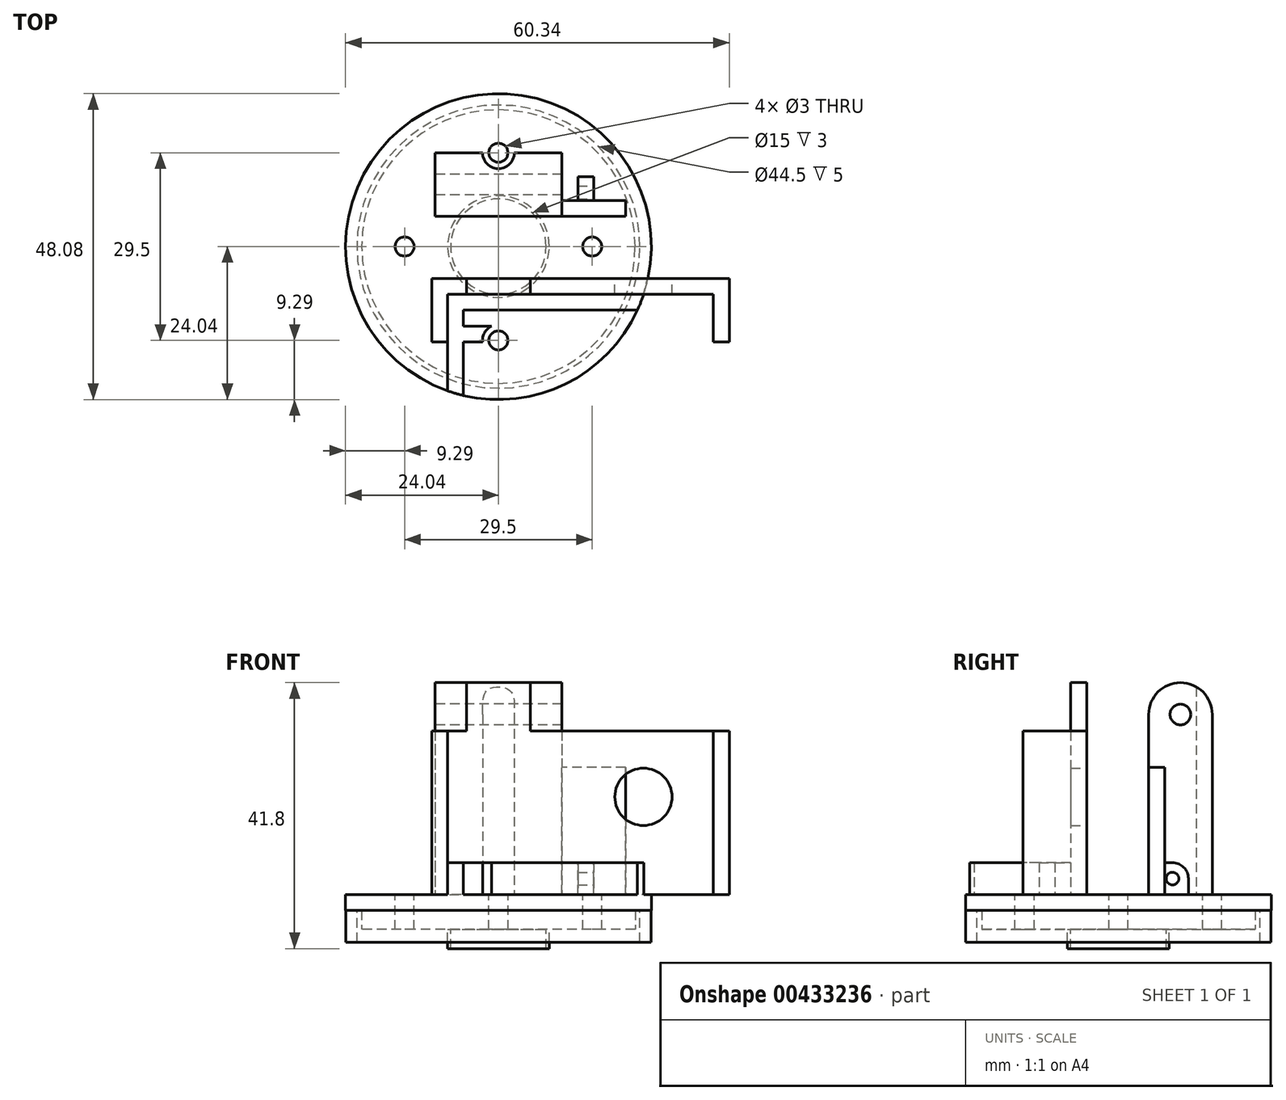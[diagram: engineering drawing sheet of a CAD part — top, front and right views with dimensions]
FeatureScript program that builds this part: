
annotation { "Feature Type Name" : "Feature", "Feature Type Description" : "" }
export const myFeature = defineFeature(function(context is Context, id is Id, definition is map)
    precondition{}
    {
        {
            var Q0;
            Q0=qCreatedBy(makeId("Top.planeOp"),FACE);
            var sketch = newSketch(context, id + "F0", { "sketchPlane" : qUnion([Q0])});
            skCircle(sketch, "E0", {"center": v(0, 0) * mm, "radius": 21.5 * mm});
            skSolve(sketch);
        }
        {
            var Q0;
            Q0 = qSketchRegion(id + "F0", true);
            extrude(context, id + "F1", {"entities" : qUnion([Q0]), "depth" : 3 * mm});
        }
        {
            var Q0;
            Q0=makeQuery(id+"F1.opExtrude","CAP_FACE",FACE,{"disambiguationData":[OSD([sQuery(id+"F0.wireOp",EDGE,"E0")])],"isStart":false});
            var sketch = newSketch(context, id + "F2", { "sketchPlane" : qUnion([Q0])});
            skLineSegment(sketch, "E1", {"start": v(0, 0) * mm, "end": v(14.75, 0) * mm, "construction": true});
            skLineSegment(sketch, "E2", {"start": v(0, 0) * mm, "end": v(0, -14.75) * mm, "construction": true});
            skLineSegment(sketch, "E3", {"start": v(0, 0) * mm, "end": v(-14.75, 0) * mm, "construction": true});
            skCircle(sketch, "E4", {"center": v(0, 14.75) * mm, "radius": 1.5 * mm});
            skCircle(sketch, "E5", {"center": v(-14.75, 0) * mm, "radius": 1.5 * mm});
            skCircle(sketch, "E6", {"center": v(14.75, 0) * mm, "radius": 1.5 * mm});
            skCircle(sketch, "E7", {"center": v(0, -14.75) * mm, "radius": 1.5 * mm});
            skLineSegment(sketch, "E8", {"start": v(0, 14.75) * mm, "end": v(0, 0) * mm, "construction": true});
            skSolve(sketch);
        }
        {
            var Q0;
            Q0 = qSketchRegion(id + "F2", true);
            extrude(context, id + "F3", {"entities" : qUnion([Q0]), "operationType" : NewBodyOperationType.REMOVE, "endBound" : BoundingType.UP_TO_NEXT, "oppositeDirection" : true, "depth" : 25 * mm});
        }
        {
            var Q0;
            Q0=makeQuery(id+"F1.opExtrude","CAP_FACE",FACE,{"disambiguationData":[OSD([sQuery(id+"F0.wireOp",EDGE,"E0")])],"isStart":false});
            var sketch = newSketch(context, id + "F4", { "sketchPlane" : qUnion([Q0])});
            skCircle(sketch, "E9", {"center": v(0, 0) * mm, "radius": 24 * mm});
            skCircle(sketch, "E10", {"center": v(0, 0) * mm, "radius": 22.25 * mm});
            skSolve(sketch);
        }
        {
            var Q0;
            Q0 = qSketchRegion(id + "F4", true);
            extrude(context, id + "F5", {"entities" : qUnion([Q0]), "oppositeDirection" : true, "depth" : 5 * mm});
        }
        {
            var Q0;
            Q0=makeQuery(id+"F5.opExtrude","CAP_FACE",FACE,{"disambiguationData":[OSD([sQuery(id+"F4.wireOp",EDGE,"E9"),sQuery(id+"F4.wireOp",EDGE,"E10")])],"isStart":true});
            var sketch = newSketch(context, id + "F6", { "sketchPlane" : qUnion([Q0])});
            skCircle(sketch, "E11", {"center": v(0, 0) * mm, "radius": 24.04 * mm});
            skLineSegment(sketch, "E12", {"start": v(0, 0) * mm, "end": v(0, 14.75) * mm, "construction": true});
            skLineSegment(sketch, "E13", {"start": v(0, 0) * mm, "end": v(14.75, 0) * mm, "construction": true});
            skLineSegment(sketch, "E14.MirrorCS", {"start": v(0, 0) * mm, "end": v(0, -14.75) * mm, "construction": true});
            skLineSegment(sketch, "E15.MirrorCS", {"start": v(0, 0) * mm, "end": v(-14.75, 0) * mm, "construction": true});
            skCircle(sketch, "E16", {"center": v(0, 14.75) * mm, "radius": 1.5 * mm});
            skCircle(sketch, "E17", {"center": v(14.75, 0) * mm, "radius": 1.5 * mm});
            skCircle(sketch, "E18.MirrorC", {"center": v(0, -14.75) * mm, "radius": 1.5 * mm});
            skCircle(sketch, "E19.MirrorC", {"center": v(-14.75, 0) * mm, "radius": 1.5 * mm});
            skSolve(sketch);
        }
        {
            var Q0;
            Q0=makeQuery(id+"F1.opExtrude","CAP_FACE",FACE,{"disambiguationData":[OSD([sQuery(id+"F0.wireOp",EDGE,"E0")])],"isStart":true});
            var sketch = newSketch(context, id + "F7", { "sketchPlane" : qUnion([Q0])});
            skCircle(sketch, "E20", {"center": v(0, 0) * mm, "radius": 8 * mm});
            skCircle(sketch, "E21", {"center": v(0, 0) * mm, "radius": 7.5 * mm});
            skSolve(sketch);
        }
        {
            var Q0;
            Q0 = qSketchRegion(id + "F7", true);
            extrude(context, id + "F8", {"entities" : qUnion([Q0]), "operationType" : NewBodyOperationType.ADD, "depth" : 3 * mm});
        }
        {
            var Q0;
            Q0 = qSketchRegion(id + "F6", true);
            extrude(context, id + "F9", {"entities" : qUnion([Q0]), "operationType" : NewBodyOperationType.ADD, "depth" : 2.5 * mm});
        }
        {
            var Q0;
            Q0=makeQuery(id+"F9.opExtrude","CAP_FACE",FACE,{"disambiguationData":[OSD([sQuery(id+"F6.wireOp",EDGE,"E11"),sQuery(id+"F6.wireOp",EDGE,"E16"),sQuery(id+"F6.wireOp",EDGE,"E17"),sQuery(id+"F6.wireOp",EDGE,"E18.MirrorC"),sQuery(id+"F6.wireOp",EDGE,"E19.MirrorC")])],"isStart":false});
            var sketch = newSketch(context, id + "F10", { "sketchPlane" : qUnion([Q0])});
            skLineSegment(sketch, "E22", {"start": v(0, 0) * mm, "end": v(0, -5) * mm, "construction": true});
            skLineSegment(sketch, "E23", {"start": v(0, -5) * mm, "end": v(-8, -5) * mm, "construction": true});
            skLineSegment(sketch, "E24.bottom", {"start": v(-8, -5) * mm, "end": v(33.8, -5) * mm});
            skLineSegment(sketch, "E24.top", {"start": v(-8, -7.5) * mm, "end": v(33.8, -7.5) * mm});
            skLineSegment(sketch, "E24.left", {"start": v(-8, -5) * mm, "end": v(-8, -7.5) * mm});
            skLineSegment(sketch, "E24.right", {"start": v(33.8, -5) * mm, "end": v(33.8, -7.5) * mm});
            skLineSegment(sketch, "E25.bottom", {"start": v(-8, -5) * mm, "end": v(-10.5, -5) * mm});
            skLineSegment(sketch, "E25.top", {"start": v(-8, -15) * mm, "end": v(-10.5, -15) * mm});
            skLineSegment(sketch, "E25.left", {"start": v(-8, -5) * mm, "end": v(-8, -15) * mm});
            skLineSegment(sketch, "E25.right", {"start": v(-10.5, -5) * mm, "end": v(-10.5, -15) * mm});
            skLineSegment(sketch, "E26.bottom", {"start": v(33.8, -5) * mm, "end": v(36.3, -5) * mm});
            skLineSegment(sketch, "E26.top", {"start": v(33.8, -15) * mm, "end": v(36.3, -15) * mm});
            skLineSegment(sketch, "E26.left", {"start": v(33.8, -5) * mm, "end": v(33.8, -15) * mm});
            skLineSegment(sketch, "E26.right", {"start": v(36.3, -5) * mm, "end": v(36.3, -15) * mm});
            skSolve(sketch);
        }
        {
            var Q0;
            Q0 = qSketchRegion(id + "F10", true);
            extrude(context, id + "F11", {"entities" : qUnion([Q0]), "operationType" : NewBodyOperationType.ADD, "depth" : 25.7 * mm});
        }
        {
            var Q0;
            Q0=makeQuery(id+"F11.opExtrude","SWEPT_FACE",FACE,{"disambiguationData":[OSD([sQuery(id+"F10.wireOp",EDGE,"E24.bottom"),sQuery(id+"F10.wireOp",EDGE,"E25.bottom"),sQuery(id+"F10.wireOp",EDGE,"E26.bottom")])]});
            var sketch = newSketch(context, id + "F12", { "sketchPlane" : qUnion([Q0])});
            skLineSegment(sketch, "E27.MirrorCS", {"start": v(-36.3, 20.85) * mm, "end": v(-27.3, 20.85) * mm, "construction": true});
            skLineSegment(sketch, "E28.MirrorCS", {"start": v(-36.3, 10.5) * mm, "end": v(-36.3, 31.2) * mm, "construction": true});
            skLineSegment(sketch, "E29.MirrorCS", {"start": v(-36.3, 5.5) * mm, "end": v(-36.3, 10.5) * mm, "construction": true});
            skLineSegment(sketch, "E30", {"start": v(-27.3, 20.85) * mm, "end": v(-22.8, 20.85) * mm, "construction": true});
            skCircle(sketch, "E31", {"center": v(-22.8, 20.85) * mm, "radius": 4.5 * mm});
            skSolve(sketch);
        }
        {
            var Q0;
            Q0=makeQuery(id+"F12.imprint","IMPRINT",FACE,{"disambiguationData":[TD([[makeQuery(id+"F12.imprint","IMPRINT",EDGE,{"derivedFrom":sQuery(id+"F12.wireOp",EDGE,"E31")}),1.0]])]});
            var Q1;
            Q1=makeQuery(id+"F11.opExtrude","SWEPT_FACE",FACE,{"disambiguationData":[OSD([sQuery(id+"F10.wireOp",EDGE,"E24.top")])]});
            extrude(context, id + "F13", {"entities" : qUnion([Q0]), "operationType" : NewBodyOperationType.REMOVE, "endBound" : BoundingType.UP_TO_SURFACE, "oppositeDirection" : true, "endBoundEntityFace" : qUnion([Q1]), "depth" : 25 * mm});
        }
        {
            var Q0;
            Q0=makeQuery(id+"F9.opExtrude","CAP_FACE",FACE,{"disambiguationData":[OSD([sQuery(id+"F6.wireOp",EDGE,"E11"),sQuery(id+"F6.wireOp",EDGE,"E16"),sQuery(id+"F6.wireOp",EDGE,"E17"),sQuery(id+"F6.wireOp",EDGE,"E18.MirrorC"),sQuery(id+"F6.wireOp",EDGE,"E19.MirrorC")])],"isStart":false});
            var sketch = newSketch(context, id + "F14", { "sketchPlane" : qUnion([Q0])});
            skLineSegment(sketch, "E32", {"start": v(-8, -15) * mm, "end": v(18.79, -15) * mm});
            skLineSegment(sketch, "E33", {"start": v(-8, -15) * mm, "end": v(-8, -12.5) * mm});
            skLineSegment(sketch, "E34", {"start": v(-8, -12.5) * mm, "end": v(20.53, -12.5) * mm});
            skLineSegment(sketch, "E35", {"start": v(-8, -12.5) * mm, "end": v(-5.5, -12.5) * mm, "construction": true});
            skCircle(sketch, "E36", {"center": v(0, -14.75) * mm, "radius": 2.5 * mm});
            skLineSegment(sketch, "E37", {"start": v(-5.5, -12.5) * mm, "end": v(-5.5, -7.5) * mm});
            skLineSegment(sketch, "E38", {"start": v(-5.5, -7.5) * mm, "end": v(-5.5, -10) * mm, "construction": true});
            skLineSegment(sketch, "E39", {"start": v(-5.5, -10) * mm, "end": v(21.86, -10) * mm});
            skLineSegment(sketch, "E40", {"start": v(20.53, -12.5) * mm, "end": v(18.03, -12.5) * mm});
            skLineSegment(sketch, "E41", {"start": v(21.86, -10) * mm, "end": v(19.36, -10) * mm});
            skLineSegment(sketch, "E42", {"start": v(19.36, -10) * mm, "end": v(18.03, -12.5) * mm});
            skLineSegment(sketch, "E43", {"start": v(-8, -15) * mm, "end": v(-8, -22.67) * mm});
            skLineSegment(sketch, "E44", {"start": v(-5.5, -12.5) * mm, "end": v(-5.5, -23.4) * mm});
            skSolve(sketch);
        }
        {
            var Q0;
            {var subQ1=sQuery(id+"F14.wireOp",EDGE,"E33");Q0=makeQuery(id+"F14.imprint","IMPRINT",FACE,{"disambiguationData":[TD([[makeQuery(id+"F14.imprint","IMPRINT",EDGE,{"derivedFrom":subQ1}),1.0]])]});}
            var Q1;
            {var subQ0=sQuery(id+"F14.wireOp",EDGE,"E37");var subQ1=sQuery(id+"F14.wireOp",EDGE,"E34");var subQ2=makeQuery(id+"F14.imprint","INTERSECT",VERTEX,{"derivedFrom":[subQ1,subQ0]});Q1=makeQuery(id+"F14.imprint","IMPRINT",FACE,{"disambiguationData":[TD([[makeQuery(id+"F14.imprint","IMPRINT",EDGE,{"disambiguationData":[TD([[subQ2,-1.0]])],"derivedFrom":subQ0}),1.0]])]});}
            var Q2;
            {var subQ7=sQuery(id+"F14.wireOp",EDGE,"E39");Q2=makeQuery(id+"F14.imprint","IMPRINT",FACE,{"disambiguationData":[TD([[makeQuery(id+"F14.imprint","IMPRINT",EDGE,{"derivedFrom":subQ7}),1.0]])]});}
            var Q3;
            {var subQ0=sQuery(id+"F14.wireOp",EDGE,"E40");Q3=makeQuery(id+"F14.imprint","IMPRINT",FACE,{"disambiguationData":[TD([[makeQuery(id+"F14.imprint","IMPRINT",EDGE,{"derivedFrom":subQ0}),-1.0]])]});}
            var Q4;
            {var subQ0=sQuery(id+"F14.wireOp",EDGE,"E40");Q4=makeQuery(id+"F14.imprint","IMPRINT",FACE,{"disambiguationData":[TD([[makeQuery(id+"F14.imprint","IMPRINT",EDGE,{"derivedFrom":subQ0}),1.0]])]});}
            var Q5;
            {var subQ0=sQuery(id+"F14.wireOp",EDGE,"E43");Q5=makeQuery(id+"F14.imprint","IMPRINT",FACE,{"disambiguationData":[TD([[makeQuery(id+"F14.imprint","IMPRINT",EDGE,{"derivedFrom":subQ0}),1.0]])]});}
            var Q6;
            {var subQ0=sQuery(id+"F14.wireOp",EDGE,"E44");var subQ1=sQuery(id+"F14.wireOp",EDGE,"E32");var subQ2=makeQuery(id+"F14.imprint","INTERSECT",VERTEX,{"derivedFrom":[subQ1,subQ0]});Q6=makeQuery(id+"F14.imprint","IMPRINT",FACE,{"disambiguationData":[TD([[makeQuery(id+"F14.imprint","IMPRINT",EDGE,{"disambiguationData":[TD([[subQ2,-1.0]])],"derivedFrom":subQ1}),1.0]])]});}
            extrude(context, id + "F15", {"entities" : qUnion([Q0, Q1, Q2, Q3, Q4, Q5, Q6]), "operationType" : NewBodyOperationType.ADD, "depth" : 5 * mm});
        }
        {
            var Q0;
            {var subQ8=sQuery(id+"F6.wireOp",EDGE,"E11");var subQ10=sQuery(id+"F6.wireOp",EDGE,"E16");var subQ11=sQuery(id+"F6.wireOp",EDGE,"E17");var subQ12=sQuery(id+"F6.wireOp",EDGE,"E19.MirrorC");var subQ13=makeQuery(id+"F9.opExtrude","CAP_FACE",FACE,{"disambiguationData":[OSD([subQ8,subQ10,subQ11,sQuery(id+"F6.wireOp",EDGE,"E18.MirrorC"),subQ12])],"isStart":false});Q0=makeQuery(id+"F15.boolean.opBoolean","SPLIT",FACE,{"disambiguationData":[TD([makeQuery(id+"F9.opExtrude","SWEPT_FACE",FACE,{"disambiguationData":[OSD([subQ10])]})])],"derivedFrom":subQ13});}
            var sketch = newSketch(context, id + "F16", { "sketchPlane" : qUnion([Q0])});
            skLineSegment(sketch, "E45", {"start": v(0, 14.75) * mm, "end": v(0, 4.75) * mm, "construction": true});
            skLineSegment(sketch, "E46", {"start": v(0, 4.75) * mm, "end": v(0, 9.75) * mm, "construction": true});
            skLineSegment(sketch, "E47.bottom", {"start": v(-10, 4.75) * mm, "end": v(10, 4.75) * mm});
            skLineSegment(sketch, "E47.top", {"start": v(-10, 14.75) * mm, "end": v(10, 14.75) * mm});
            skLineSegment(sketch, "E47.left", {"start": v(-10, 4.75) * mm, "end": v(-10, 14.75) * mm});
            skLineSegment(sketch, "E47.right", {"start": v(10, 4.75) * mm, "end": v(10, 14.75) * mm});
            skPoint(sketch, "E47.middle", {"position": v(0, 9.75) * mm});
            skCircle(sketch, "E48", {"center": v(0, 14.75) * mm, "radius": 2.5 * mm});
            skSolve(sketch);
        }
        {
            var Q0;
            Q0=makeQuery(id+"F16.imprint","IMPRINT",FACE,{"disambiguationData":[TD([[makeQuery(id+"F16.imprint","IMPRINT",EDGE,{"derivedFrom":sQuery(id+"F16.wireOp",EDGE,"E47.bottom")}),1.0]])]});
            extrude(context, id + "F17", {"entities" : qUnion([Q0]), "operationType" : NewBodyOperationType.ADD, "depth" : 33.3 * mm});
        }
        {
            var Q0;
            Q0=makeQuery(id+"F17.opExtrude","SWEPT_FACE",FACE,{"disambiguationData":[OSD([sQuery(id+"F16.wireOp",EDGE,"E47.left")])]});
            var sketch = newSketch(context, id + "F18", { "sketchPlane" : qUnion([Q0])});
            skLineSegment(sketch, "E49", {"start": v(-9.75, 38.8) * mm, "end": v(-9.75, 28.8) * mm, "construction": true});
            skPoint(sketch, "E49.endSnap0", {"position": v(-9.75, 38.8) * mm});
            skCircle(sketch, "E50", {"center": v(-9.75, 33.8) * mm, "radius": 5 * mm});
            skCircle(sketch, "E51", {"center": v(-9.75, 33.8) * mm, "radius": 1.63 * mm});
            skSolve(sketch);
        }
        {
            var Q0;
            Q0=makeQuery(id+"F18.imprint","IMPRINT",FACE,{"disambiguationData":[TD([[makeQuery(id+"F18.imprint","IMPRINT",EDGE,{"derivedFrom":sQuery(id+"F18.wireOp",EDGE,"E51")}),1.0]])]});
            var Q1;
            {var subQ0=sQuery(id+"F18.wireOp",EDGE,"E50");var subQ1=sQuery(id+"F16.wireOp",EDGE,"E47.left");var subQ2=makeQuery(id+"F17.opExtrude","CAP_EDGE",EDGE,{"disambiguationData":[OSD([subQ1])],"isStart":false});var subQ3=makeQuery(id+"F18.imprint","INTERSECT",VERTEX,{"derivedFrom":[subQ2,subQ0]});Q1=makeQuery(id+"F18.imprint","IMPRINT",FACE,{"disambiguationData":[TD([[makeQuery(id+"F18.imprint","IMPRINT",EDGE,{"disambiguationData":[TD([[subQ3,-1.0]])],"derivedFrom":subQ0}),-1.0]])]});}
            var Q2;
            {var subQ0=sQuery(id+"F18.wireOp",EDGE,"E50");var subQ1=sQuery(id+"F16.wireOp",EDGE,"E47.left");var subQ2=makeQuery(id+"F17.opExtrude","CAP_EDGE",EDGE,{"disambiguationData":[OSD([subQ1])],"isStart":false});var subQ3=makeQuery(id+"F18.imprint","INTERSECT",VERTEX,{"derivedFrom":[subQ2,subQ0]});Q2=makeQuery(id+"F18.imprint","IMPRINT",FACE,{"disambiguationData":[TD([[makeQuery(id+"F18.imprint","IMPRINT",EDGE,{"disambiguationData":[TD([[subQ3,1.0]])],"derivedFrom":subQ0}),-1.0]])]});}
            var Q3;
            Q3=makeQuery(id+"F17.opExtrude","SWEPT_FACE",FACE,{"disambiguationData":[OSD([sQuery(id+"F16.wireOp",EDGE,"E47.right")])]});
            extrude(context, id + "F19", {"entities" : qUnion([Q0, Q1, Q2]), "operationType" : NewBodyOperationType.REMOVE, "endBound" : BoundingType.UP_TO_SURFACE, "oppositeDirection" : true, "endBoundEntityFace" : qUnion([Q3]), "depth" : 25 * mm});
        }
        {
            var Q0;
            Q0=makeQuery(id+"F11.opExtrude","CAP_FACE",FACE,{"disambiguationData":[OSD([sQuery(id+"F10.wireOp",EDGE,"E24.bottom"),sQuery(id+"F10.wireOp",EDGE,"E24.top"),sQuery(id+"F10.wireOp",EDGE,"E25.bottom"),sQuery(id+"F10.wireOp",EDGE,"E25.top"),sQuery(id+"F10.wireOp",EDGE,"E25.left"),sQuery(id+"F10.wireOp",EDGE,"E25.right"),sQuery(id+"F10.wireOp",EDGE,"E26.bottom"),sQuery(id+"F10.wireOp",EDGE,"E26.top"),sQuery(id+"F10.wireOp",EDGE,"E26.left"),sQuery(id+"F10.wireOp",EDGE,"E26.right")])],"isStart":false});
            var sketch = newSketch(context, id + "F20", { "sketchPlane" : qUnion([Q0])});
            skLineSegment(sketch, "E52", {"start": v(0, 0) * mm, "end": v(0, -5) * mm, "construction": true});
            skLineSegment(sketch, "E53", {"start": v(0, -5) * mm, "end": v(-5, -5) * mm, "construction": true});
            skLineSegment(sketch, "E54.bottom", {"start": v(-5, -5) * mm, "end": v(5, -5) * mm});
            skLineSegment(sketch, "E54.top", {"start": v(-5, -7.5) * mm, "end": v(5, -7.5) * mm});
            skLineSegment(sketch, "E54.left", {"start": v(-5, -5) * mm, "end": v(-5, -7.5) * mm});
            skLineSegment(sketch, "E54.right", {"start": v(5, -5) * mm, "end": v(5, -7.5) * mm});
            skSolve(sketch);
        }
        {
            var Q0;
            Q0 = qSketchRegion(id + "F20", true);
            extrude(context, id + "F21", {"entities" : qUnion([Q0]), "operationType" : NewBodyOperationType.ADD, "depth" : 7.6 * mm});
        }
        {
            var Q0;
            {var subQ8=sQuery(id+"F6.wireOp",EDGE,"E11");var subQ10=sQuery(id+"F6.wireOp",EDGE,"E16");var subQ11=sQuery(id+"F6.wireOp",EDGE,"E17");var subQ12=sQuery(id+"F6.wireOp",EDGE,"E19.MirrorC");var subQ13=makeQuery(id+"F9.opExtrude","CAP_FACE",FACE,{"disambiguationData":[OSD([subQ8,subQ10,subQ11,sQuery(id+"F6.wireOp",EDGE,"E18.MirrorC"),subQ12])],"isStart":false});Q0=makeQuery(id+"F15.boolean.opBoolean","SPLIT",FACE,{"disambiguationData":[TD([makeQuery(id+"F9.opExtrude","SWEPT_FACE",FACE,{"disambiguationData":[OSD([subQ10])]})])],"derivedFrom":subQ13});}
            var sketch = newSketch(context, id + "F22", { "sketchPlane" : qUnion([Q0])});
            skLineSegment(sketch, "E55.bottom", {"start": v(12.5, 6) * mm, "end": v(15, 6) * mm, "construction": true});
            skLineSegment(sketch, "E55.top", {"start": v(12.5, 11) * mm, "end": v(15, 11) * mm, "construction": true});
            skLineSegment(sketch, "E55.left", {"start": v(12.5, 6) * mm, "end": v(12.5, 11) * mm, "construction": true});
            skLineSegment(sketch, "E55.right", {"start": v(15, 6) * mm, "end": v(15, 11) * mm, "construction": true});
            skLineSegment(sketch, "E56.bottom", {"start": v(12.5, 6) * mm, "end": v(15, 6) * mm});
            skLineSegment(sketch, "E56.top", {"start": v(12.5, 11) * mm, "end": v(15, 11) * mm});
            skLineSegment(sketch, "E56.left", {"start": v(12.5, 6) * mm, "end": v(12.5, 11) * mm});
            skLineSegment(sketch, "E56.right", {"start": v(15, 6) * mm, "end": v(15, 11) * mm});
            skLineSegment(sketch, "E57", {"start": v(12.5, 8.5) * mm, "end": v(10, 8.5) * mm, "construction": true});
            skLineSegment(sketch, "E58", {"start": v(10, 8.5) * mm, "end": v(10, 4.75) * mm, "construction": true});
            skSolve(sketch);
        }
        {
            var Q0;
            Q0 = qSketchRegion(id + "F22", true);
            extrude(context, id + "F23", {"entities" : qUnion([Q0]), "operationType" : NewBodyOperationType.ADD, "depth" : 5 * mm});
        }
        {
            var Q0;
            Q0=makeQuery(id+"F23.opExtrude","SWEPT_FACE",FACE,{"disambiguationData":[OSD([sQuery(id+"F22.wireOp",EDGE,"E56.right")])]});
            var sketch = newSketch(context, id + "F24", { "sketchPlane" : qUnion([Q0])});
            skLineSegment(sketch, "E59", {"start": v(6, 8) * mm, "end": v(11, 8) * mm, "construction": true});
            skCircle(sketch, "E60", {"center": v(8.5, 8) * mm, "radius": 1 * mm});
            skSolve(sketch);
        }
        {
            var Q0;
            Q0 = qSketchRegion(id + "F24", true);
            var Q1;
            Q1=makeQuery(id+"F23.opExtrude","SWEPT_FACE",FACE,{"disambiguationData":[OSD([sQuery(id+"F22.wireOp",EDGE,"E56.left")])]});
            extrude(context, id + "F25", {"entities" : qUnion([Q0]), "operationType" : NewBodyOperationType.REMOVE, "endBound" : BoundingType.UP_TO_SURFACE, "oppositeDirection" : true, "endBoundEntityFace" : qUnion([Q1]), "depth" : 25 * mm});
        }
        {
            var Q0;
            Q0=makeQuery(id+"F17.opExtrude","SWEPT_FACE",FACE,{"disambiguationData":[OSD([sQuery(id+"F16.wireOp",EDGE,"E47.right")])]});
            var sketch = newSketch(context, id + "F26", { "sketchPlane" : qUnion([Q0])});
            skLineSegment(sketch, "E61.bottom", {"start": v(4.75, 5.5) * mm, "end": v(7.25, 5.5) * mm});
            skLineSegment(sketch, "E61.top", {"start": v(4.75, 25.5) * mm, "end": v(7.25, 25.5) * mm});
            skLineSegment(sketch, "E61.left", {"start": v(4.75, 5.5) * mm, "end": v(4.75, 25.5) * mm});
            skLineSegment(sketch, "E61.right", {"start": v(7.25, 5.5) * mm, "end": v(7.25, 25.5) * mm});
            skSolve(sketch);
        }
        {
            var Q0;
            Q0 = qSketchRegion(id + "F26", true);
            extrude(context, id + "F27", {"entities" : qUnion([Q0]), "operationType" : NewBodyOperationType.ADD, "depth" : 10 * mm});
        }
        {
            var Q0;
            Q0=makeQuery(id+"F23.opExtrude","CAP_EDGE",EDGE,{"disambiguationData":[OSD([sQuery(id+"F22.wireOp",EDGE,"E56.top")])],"isStart":false});
            fillet(context, id + "F28", {"entities" : qUnion([Q0]), "radius" : 2.5 * mm, "tangentPropagation" : true, "allowEdgeOverflow" : false});
        }
    });
